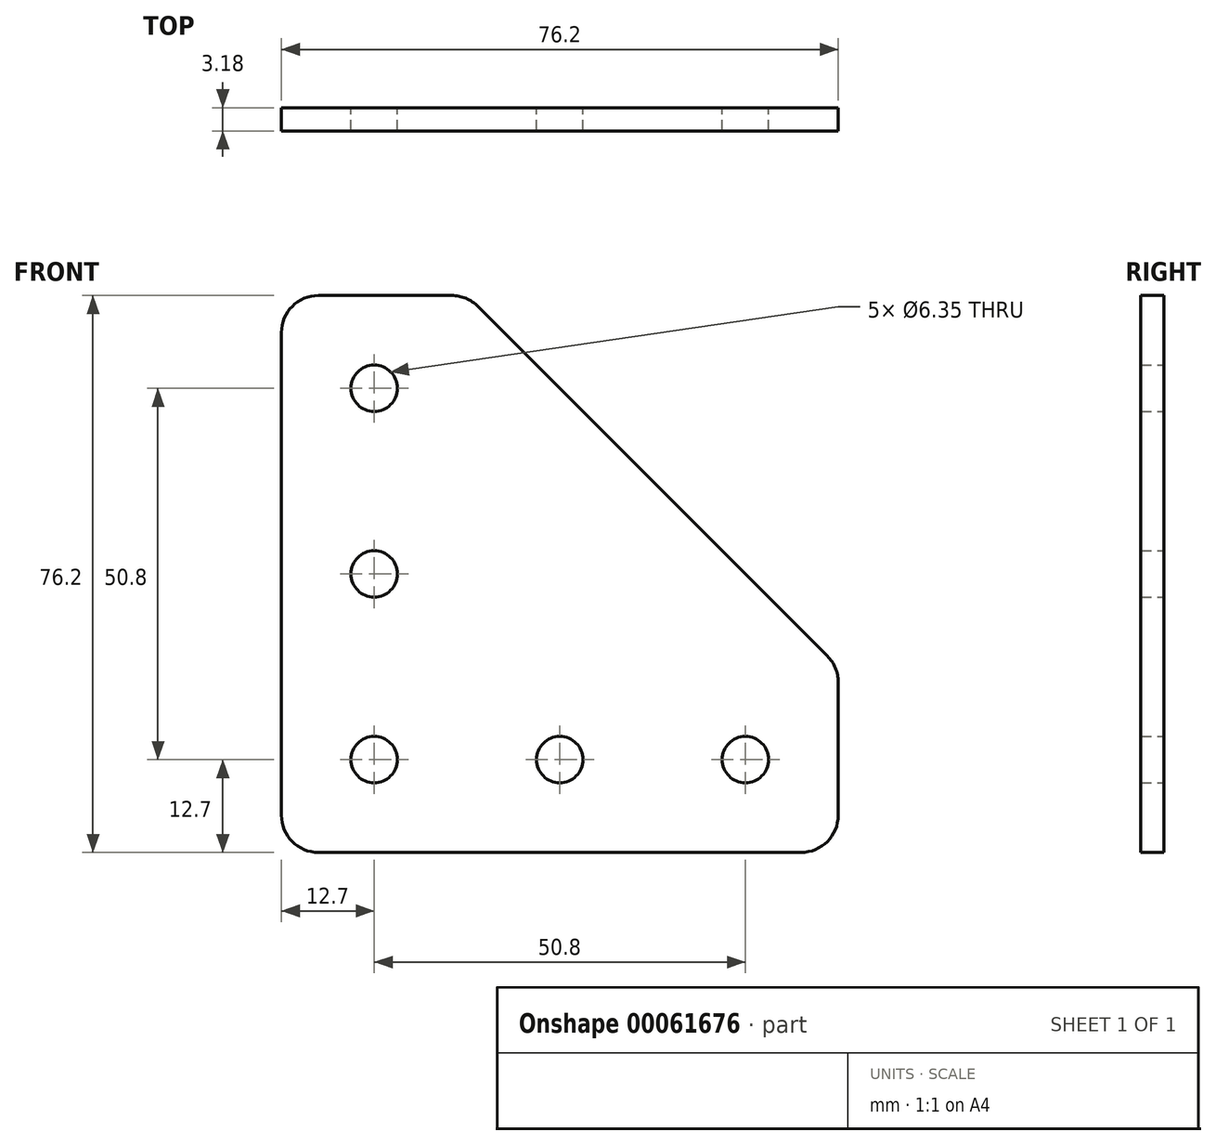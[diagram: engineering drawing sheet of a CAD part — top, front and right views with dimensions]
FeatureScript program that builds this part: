
annotation { "Feature Type Name" : "Feature", "Feature Type Description" : "" }
export const myFeature = defineFeature(function(context is Context, id is Id, definition is map)
    precondition{}
    {
        {
            var Q0;
            Q0=qCreatedBy(makeId("Front.planeOp"),FACE);
            var sketch = newSketch(context, id + "F0", { "sketchPlane" : qUnion([Q0])});
            skLineSegment(sketch, "E0.bottom", {"start": v(0, 0) * mm, "end": v(76.2, 0) * mm});
            skLineSegment(sketch, "E0.top", {"start": v(0, 76.2) * mm, "end": v(76.2, 76.2) * mm});
            skLineSegment(sketch, "E0.left", {"start": v(0, 0) * mm, "end": v(0, 76.2) * mm});
            skLineSegment(sketch, "E0.right", {"start": v(76.2, 0) * mm, "end": v(76.2, 76.2) * mm});
            skSolve(sketch);
        }
        {
            var Q0;
            Q0=makeQuery(id+"F0.imprint","IMPRINT",FACE,{"disambiguationData":[TD([[makeQuery(id+"F0.imprint","IMPRINT",EDGE,{"derivedFrom":sQuery(id+"F0.wireOp",EDGE,"E0.bottom")}),1.0]])]});
            extrude(context, id + "F1", {"entities" : qUnion([Q0]), "depth" : 3.17 * mm});
        }
        {
            var Q0;
            Q0=makeQuery(id+"F1.opExtrude","SWEPT_EDGE",EDGE,{"disambiguationData":[OSD([sQuery(id+"F0.wireOp",EDGE,"E0.top"),sQuery(id+"F0.wireOp",EDGE,"E0.right")])]});
            chamfer(context, id + "F2", {"entities" : qUnion([Q0]), "width" : 50.8 * mm, "tangentPropagation" : true});
        }
        {
            var Q0;
            Q0=makeQuery(id+"F1.opExtrude","SWEPT_EDGE",EDGE,{"disambiguationData":[OSD([sQuery(id+"F0.wireOp",EDGE,"E0.top"),sQuery(id+"F0.wireOp",EDGE,"E0.left")])]});
            var Q1;
            {var subQ0=sQuery(id+"F0.wireOp",EDGE,"E0.top");Q1=makeQuery(id+"F2.opChamfer","BLEND_EDGE",EDGE,{"blendedFrom":[makeQuery(id+"F1.opExtrude","SWEPT_EDGE",EDGE,{"disambiguationData":[OSD([subQ0,sQuery(id+"F0.wireOp",EDGE,"E0.right")])]}),makeQuery(id+"F1.opExtrude","SWEPT_FACE",FACE,{"disambiguationData":[OSD([subQ0])]})],"blendedInto":[makeQuery(id+"F1.opExtrude","SWEPT_FACE",FACE,{"disambiguationData":[OSD([subQ0])]})]});}
            var Q2;
            {var subQ0=sQuery(id+"F0.wireOp",EDGE,"E0.right");Q2=makeQuery(id+"F2.opChamfer","BLEND_EDGE",EDGE,{"blendedFrom":[makeQuery(id+"F1.opExtrude","SWEPT_EDGE",EDGE,{"disambiguationData":[OSD([sQuery(id+"F0.wireOp",EDGE,"E0.top"),subQ0])]}),makeQuery(id+"F1.opExtrude","SWEPT_FACE",FACE,{"disambiguationData":[OSD([subQ0])]})],"blendedInto":[makeQuery(id+"F1.opExtrude","SWEPT_FACE",FACE,{"disambiguationData":[OSD([subQ0])]})]});}
            var Q3;
            Q3=makeQuery(id+"F1.opExtrude","SWEPT_EDGE",EDGE,{"disambiguationData":[OSD([sQuery(id+"F0.wireOp",EDGE,"E0.bottom"),sQuery(id+"F0.wireOp",EDGE,"E0.right")])]});
            var Q4;
            Q4=makeQuery(id+"F1.opExtrude","SWEPT_EDGE",EDGE,{"disambiguationData":[OSD([sQuery(id+"F0.wireOp",EDGE,"E0.bottom"),sQuery(id+"F0.wireOp",EDGE,"E0.left")])]});
            fillet(context, id + "F3", {"entities" : qUnion([Q0, Q1, Q2, Q3, Q4]), "radius" : 5.08 * mm, "tangentPropagation" : true, "allowEdgeOverflow" : false});
        }
        {
            var Q0;
            Q0=makeQuery(id+"F1.opExtrude","CAP_FACE",FACE,{"disambiguationData":[OSD([sQuery(id+"F0.wireOp",EDGE,"E0.bottom"),sQuery(id+"F0.wireOp",EDGE,"E0.top"),sQuery(id+"F0.wireOp",EDGE,"E0.left"),sQuery(id+"F0.wireOp",EDGE,"E0.right")])],"isStart":true});
            var sketch = newSketch(context, id + "F4", { "sketchPlane" : qUnion([Q0])});
            skPoint(sketch, "E1", {"position": v(-12.7, 12.7) * mm});
            skPoint(sketch, "E2", {"position": v(-12.7, 38.1) * mm});
            skPoint(sketch, "E3", {"position": v(-12.7, 63.5) * mm});
            skPoint(sketch, "E4", {"position": v(-38.1, 12.7) * mm});
            skPoint(sketch, "E5", {"position": v(-63.5, 12.7) * mm});
            skSolve(sketch);
        }
        {
            var Q0;
            Q0=sQuery(id+"F4.wireOp",VERTEX,"E1");
            var Q1;
            Q1=sQuery(id+"F4.wireOp",VERTEX,"E2");
            var Q2;
            Q2=sQuery(id+"F4.wireOp",VERTEX,"E3");
            var Q3;
            Q3=sQuery(id+"F4.wireOp",VERTEX,"E4");
            var Q4;
            Q4=sQuery(id+"F4.wireOp",VERTEX,"E5");
            var Q5;
            Q5=makeQuery(id+"F1.opExtrude","SWEPT_BODY",BODY,{"disambiguationData":[OSD([sQuery(id+"F0.wireOp",EDGE,"E0.bottom"),sQuery(id+"F0.wireOp",EDGE,"E0.top"),sQuery(id+"F0.wireOp",EDGE,"E0.left"),sQuery(id+"F0.wireOp",EDGE,"E0.right")])]});
            hole(context, id + "F5", {"style" : HoleStyle.SIMPLE, "holeDiameter" : 6.35 * mm, "endStyle" : HoleEndStyle.THROUGH, "locations" : qUnion([Q0, Q1, Q2, Q3, Q4]), "scope" : qUnion([Q5])});
        }
    });
